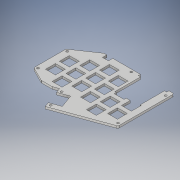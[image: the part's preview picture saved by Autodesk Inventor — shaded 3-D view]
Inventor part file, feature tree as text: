
AUTODESK INVENTOR PART (.ipt)
format: ipt  version: 2017 (Build 210142000, 142)  size: 260,096 bytes
history: native  units: in
note: dims shown in document units (in); Inventor stores cm internally (conversion verified against a paired STEP export)
features: other x3, extrude x3, sketch x3
ambient origin geometry x8: Origin, YZ Plane, XZ Plane, XY Plane, X Axis, Y Axis, Z Axis, Center Point
bodies: Body1 (feature_tree)
feature tree (9):
  other  "k2_l1.ipt"
  extrude  "Extrusion3"  Depth=1.2992in
  extrude  "Extrusion4"  Depth=0.1575in
  extrude  "Extrusion7"  Depth=0.1181in
  other  "Solid3::k2_l1.ipt"
  other  "TaggingFeature3"
  sketch  "Sketch3"  dims[d21=0.3937in d22=1.2992in]
  sketch  "Sketch4"  dims[d23=0.1181in d24=0.1575in]
  sketch  "Sketch8"  dims[d25=0.2756in d26=0.1181in d27=0.3937in d28=0.0in d29=1.378in d30=0.3937in d31=0.0in d41=0.315in d42=0.0in d43=0.5906in d44=0.748in d45=0.2756in]
